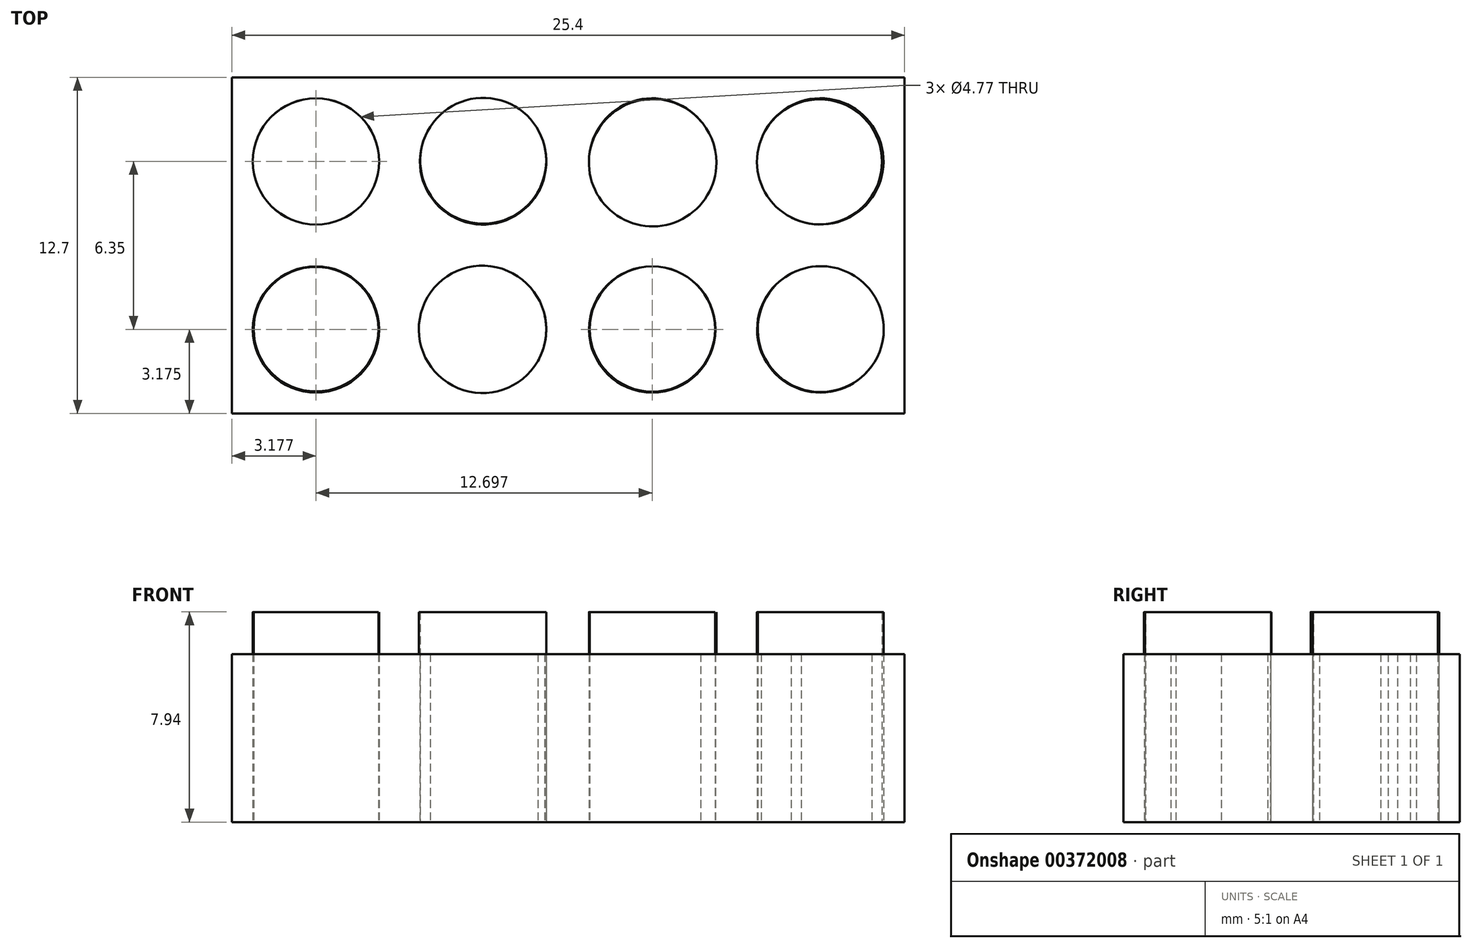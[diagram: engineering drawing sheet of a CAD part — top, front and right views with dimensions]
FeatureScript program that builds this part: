
annotation { "Feature Type Name" : "Feature", "Feature Type Description" : "" }
export const myFeature = defineFeature(function(context is Context, id is Id, definition is map)
    precondition{}
    {
        {
            var Q0;
            Q0=qCreatedBy(makeId("Top.planeOp"),FACE);
            var sketch = newSketch(context, id + "F0", { "sketchPlane" : qUnion([Q0])});
            skLineSegment(sketch, "E0.bottom", {"start": v(-12.5, 5.1) * mm, "end": v(12.9, 5.1) * mm});
            skLineSegment(sketch, "E0.top", {"start": v(-12.5, -7.6) * mm, "end": v(12.9, -7.6) * mm});
            skLineSegment(sketch, "E0.left", {"start": v(-12.5, 5.1) * mm, "end": v(-12.5, -7.6) * mm});
            skLineSegment(sketch, "E0.right", {"start": v(12.9, 5.1) * mm, "end": v(12.9, -7.6) * mm});
            skLineSegment(sketch, "E1", {"start": v(-12.5, -1.26) * mm, "end": v(12.9, -1.26) * mm, "construction": true});
            skLineSegment(sketch, "E2", {"start": v(0.2, 5.1) * mm, "end": v(0.2, -7.6) * mm, "construction": true});
            skLineSegment(sketch, "E3", {"start": v(-6.19, 7.35) * mm, "end": v(-6.19, -7.6) * mm, "construction": true});
            skLineSegment(sketch, "E4", {"start": v(6.55, 7.17) * mm, "end": v(6.55, -7.6) * mm, "construction": true});
            skLineSegment(sketch, "E5", {"start": v(-9.32, 6.74) * mm, "end": v(-9.32, -7.6) * mm, "construction": true});
            skLineSegment(sketch, "E6", {"start": v(-14.9, -4.43) * mm, "end": v(12.9, -4.43) * mm, "construction": true});
            skLineSegment(sketch, "E7", {"start": v(-15.17, 1.92) * mm, "end": v(12.9, 1.92) * mm, "construction": true});
            skCircle(sketch, "E8", {"center": v(-9.32, 1.92) * mm, "radius": 2.39 * mm});
            skCircle(sketch, "E9", {"center": v(-9.32, -4.43) * mm, "radius": 2.39 * mm});
            skLineSegment(sketch, "E10", {"start": v(-3.01, 8.99) * mm, "end": v(-3.01, -7.6) * mm, "construction": true});
            skCircle(sketch, "E11", {"center": v(-3.01, 1.92) * mm, "radius": 2.39 * mm});
            skCircle(sketch, "E12", {"center": v(-3.01, -4.43) * mm, "radius": 2.39 * mm});
            skLineSegment(sketch, "E13", {"start": v(3.37, 8.51) * mm, "end": v(3.37, -7.6) * mm, "construction": true});
            skLineSegment(sketch, "E14", {"start": v(9.72, 8.86) * mm, "end": v(9.72, -7.6) * mm, "construction": true});
            skCircle(sketch, "E15", {"center": v(3.37, 1.92) * mm, "radius": 2.39 * mm});
            skLineSegment(sketch, "E16", {"start": v(16.1, 8.86) * mm, "end": v(16.1, -7.6) * mm, "construction": true});
            skCircle(sketch, "E17", {"center": v(9.72, 1.92) * mm, "radius": 2.39 * mm});
            skCircle(sketch, "E18", {"center": v(3.37, -4.43) * mm, "radius": 2.39 * mm});
            skCircle(sketch, "E19", {"center": v(9.72, -4.43) * mm, "radius": 2.39 * mm});
            skSolve(sketch);
        }
        {
            var Q0;
            Q0=makeQuery(id+"F0.imprint","IMPRINT",FACE,{"disambiguationData":[TD([[makeQuery(id+"F0.imprint","IMPRINT",EDGE,{"derivedFrom":sQuery(id+"F0.wireOp",EDGE,"E0.bottom")}),-1.0]])]});
            extrude(context, id + "F1", {"entities" : qUnion([Q0]), "depth" : 6.35 * mm});
        }
        {
            var Q0;
            Q0=qCreatedBy(makeId("Top.planeOp"),FACE);
            var sketch = newSketch(context, id + "F2", { "sketchPlane" : qUnion([Q0])});
            skCircle(sketch, "E20", {"center": v(-9.32, 1.91) * mm, "radius": 2.38 * mm});
            skPoint(sketch, "E20.first.point", {"position": v(-10.3, 4.09) * mm});
            skPoint(sketch, "E20.second.point", {"position": v(-8.4, -0.29) * mm});
            skPoint(sketch, "E20.third.point", {"position": v(-6.94, 1.95) * mm});
            skCircle(sketch, "E21", {"center": v(-3, 1.94) * mm, "radius": 2.38 * mm});
            skPoint(sketch, "E21.first.point", {"position": v(-3.86, 4.16) * mm});
            skPoint(sketch, "E21.second.point", {"position": v(-5.36, 1.64) * mm});
            skPoint(sketch, "E21.third.point", {"position": v(-1.13, 0.48) * mm});
            skCircle(sketch, "E22", {"center": v(3.39, 1.87) * mm, "radius": 2.4 * mm});
            skPoint(sketch, "E22.first.point", {"position": v(2.13, 3.91) * mm});
            skPoint(sketch, "E22.second.point", {"position": v(1, 1.53) * mm});
            skPoint(sketch, "E22.third.point", {"position": v(1.22, 2.9) * mm});
            skCircle(sketch, "E23", {"center": v(9.7, 1.9) * mm, "radius": 2.36 * mm});
            skPoint(sketch, "E23.first.point", {"position": v(10.98, 3.88) * mm});
            skPoint(sketch, "E23.second.point", {"position": v(7.41, 2.51) * mm});
            skPoint(sketch, "E23.third.point", {"position": v(10.07, -0.43) * mm});
            skCircle(sketch, "E24", {"center": v(-9.32, -4.42) * mm, "radius": 2.35 * mm});
            skPoint(sketch, "E24.first.point", {"position": v(-8.51, -2.21) * mm});
            skPoint(sketch, "E24.second.point", {"position": v(-11.52, -5.26) * mm});
            skPoint(sketch, "E24.third.point", {"position": v(-7.53, -5.96) * mm});
            skCircle(sketch, "E25", {"center": v(-3.03, -4.43) * mm, "radius": 2.4 * mm});
            skPoint(sketch, "E25.first.point", {"position": v(-3.26, -2.04) * mm});
            skPoint(sketch, "E25.second.point", {"position": v(-0.81, -5.36) * mm});
            skPoint(sketch, "E25.third.point", {"position": v(-4.77, -6.1) * mm});
            skCircle(sketch, "E26", {"center": v(3.38, -4.42) * mm, "radius": 2.37 * mm});
            skPoint(sketch, "E26.first.point", {"position": v(4.02, -2.14) * mm});
            skPoint(sketch, "E26.second.point", {"position": v(2.16, -6.45) * mm});
            skPoint(sketch, "E26.third.point", {"position": v(4.33, -6.59) * mm});
            skCircle(sketch, "E27", {"center": v(9.74, -4.42) * mm, "radius": 2.38 * mm});
            skPoint(sketch, "E27.first.point", {"position": v(9.37, -2.07) * mm});
            skPoint(sketch, "E27.second.point", {"position": v(9.9, -6.8) * mm});
            skPoint(sketch, "E27.third.point", {"position": v(11.93, -5.36) * mm});
            skSolve(sketch);
        }
        {
            var Q0;
            Q0=makeQuery(id+"F2.imprint","IMPRINT",FACE,{"disambiguationData":[TD([[makeQuery(id+"F2.imprint","IMPRINT",EDGE,{"derivedFrom":sQuery(id+"F2.wireOp",EDGE,"E20")}),1.0]])]});
            var Q1;
            Q1=makeQuery(id+"F2.imprint","IMPRINT",FACE,{"disambiguationData":[TD([[makeQuery(id+"F2.imprint","IMPRINT",EDGE,{"derivedFrom":sQuery(id+"F2.wireOp",EDGE,"E24")}),1.0]])]});
            var Q2;
            Q2=makeQuery(id+"F2.imprint","IMPRINT",FACE,{"disambiguationData":[TD([[makeQuery(id+"F2.imprint","IMPRINT",EDGE,{"derivedFrom":sQuery(id+"F2.wireOp",EDGE,"E25")}),1.0]])]});
            var Q3;
            Q3=makeQuery(id+"F2.imprint","IMPRINT",FACE,{"disambiguationData":[TD([[makeQuery(id+"F2.imprint","IMPRINT",EDGE,{"derivedFrom":sQuery(id+"F2.wireOp",EDGE,"E21")}),1.0]])]});
            var Q4;
            Q4=makeQuery(id+"F2.imprint","IMPRINT",FACE,{"disambiguationData":[TD([[makeQuery(id+"F2.imprint","IMPRINT",EDGE,{"derivedFrom":sQuery(id+"F2.wireOp",EDGE,"E22")}),1.0]])]});
            var Q5;
            Q5=makeQuery(id+"F2.imprint","IMPRINT",FACE,{"disambiguationData":[TD([[makeQuery(id+"F2.imprint","IMPRINT",EDGE,{"derivedFrom":sQuery(id+"F2.wireOp",EDGE,"E26")}),1.0]])]});
            var Q6;
            Q6=makeQuery(id+"F2.imprint","IMPRINT",FACE,{"disambiguationData":[TD([[makeQuery(id+"F2.imprint","IMPRINT",EDGE,{"derivedFrom":sQuery(id+"F2.wireOp",EDGE,"E27")}),1.0]])]});
            var Q7;
            Q7=makeQuery(id+"F2.imprint","IMPRINT",FACE,{"disambiguationData":[TD([[makeQuery(id+"F2.imprint","IMPRINT",EDGE,{"derivedFrom":sQuery(id+"F2.wireOp",EDGE,"E23")}),1.0]])]});
            extrude(context, id + "F3", {"entities" : qUnion([Q0, Q1, Q2, Q3, Q4, Q5, Q6, Q7]), "operationType" : NewBodyOperationType.ADD, "depth" : 7.94 * mm});
        }
    });
